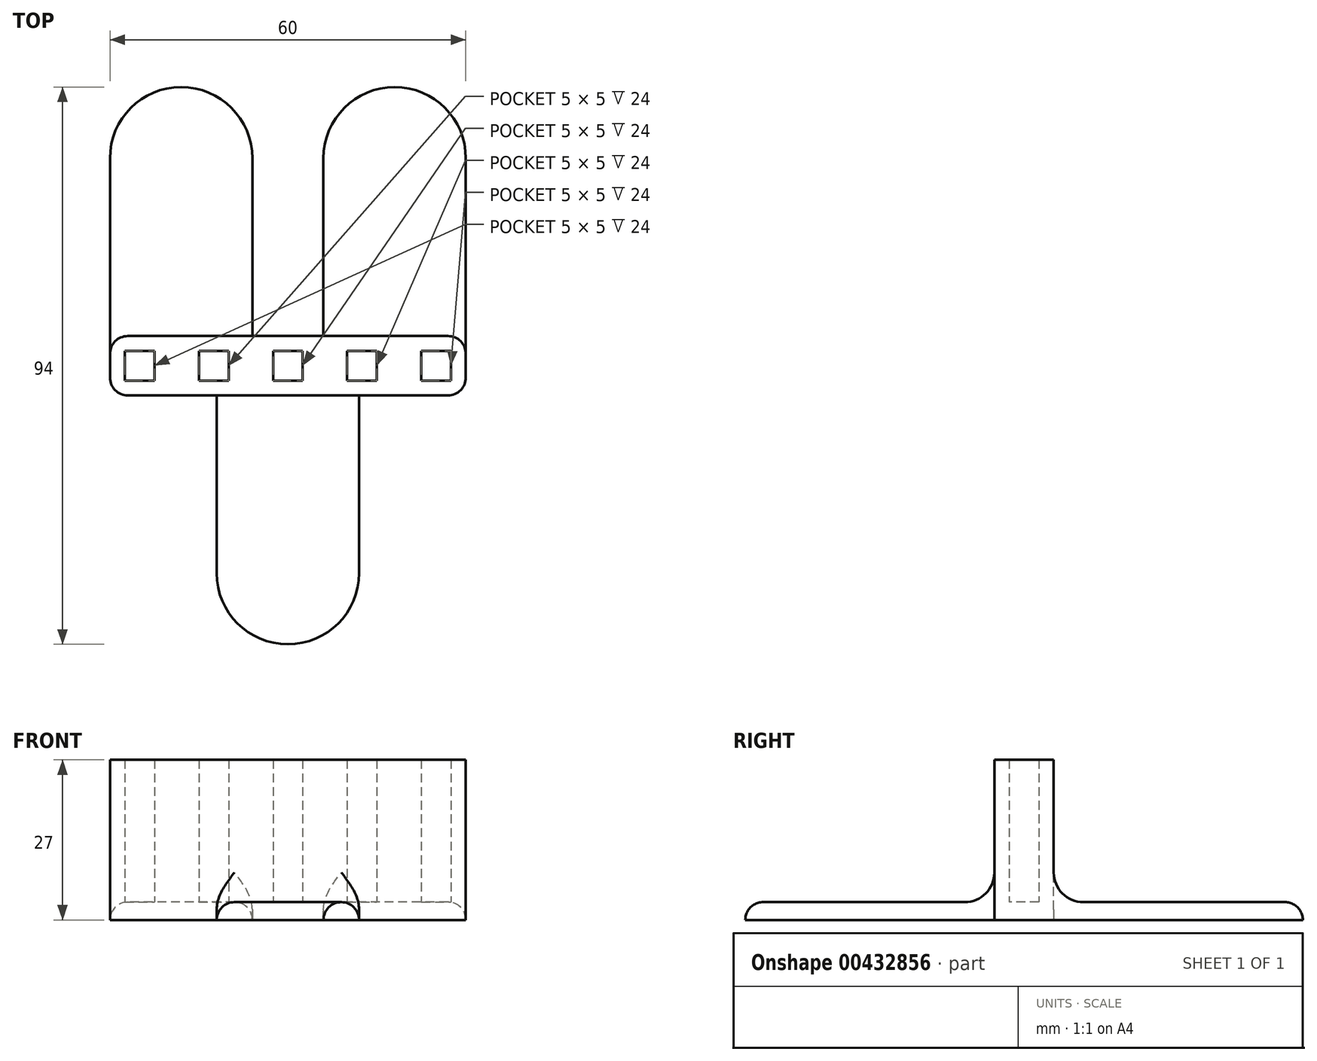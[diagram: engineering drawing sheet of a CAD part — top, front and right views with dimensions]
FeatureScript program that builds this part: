
annotation { "Feature Type Name" : "Feature", "Feature Type Description" : "" }
export const myFeature = defineFeature(function(context is Context, id is Id, definition is map)
    precondition{}
    {
        {
            var Q0;
            Q0=qCreatedBy(makeId("Top.planeOp"),FACE);
            var sketch = newSketch(context, id + "F0", { "sketchPlane" : qUnion([Q0])});
            skLineSegment(sketch, "E0.bottom", {"start": v(-12, -5) * mm, "end": v(-30, -5) * mm});
            skLineSegment(sketch, "E0.top", {"start": v(0, 5) * mm, "end": v(-6, 5) * mm});
            skLineSegment(sketch, "E0.right", {"start": v(-30, -5) * mm, "end": v(-30, 5) * mm});
            skLineSegment(sketch, "E1.left", {"start": v(-30, 5) * mm, "end": v(-30, 35) * mm});
            skLineSegment(sketch, "E1.right", {"start": v(-6, 5) * mm, "end": v(-6, 35) * mm});
            skLineSegment(sketch, "E2.right", {"start": v(-12, -5) * mm, "end": v(-12, -35) * mm});
            skArc(sketch, "E3", {"start": v(-12, -35) * mm, "mid": v(-8.49, -43.49) * mm, "end": v(0, -47) * mm});
            skArc(sketch, "E4", {"start": v(-6, 35) * mm, "mid": v(-18, 47) * mm, "end": v(-30, 35) * mm});
            skPoint(sketch, "E2.left.start.orphan", {"position": v(0, -5) * mm});
            skPoint(sketch, "E5", {"position": v(-30, 0) * mm});
            skLineSegment(sketch, "E6", {"start": v(0, -5) * mm, "end": v(0, -35) * mm, "construction": true});
            skLineSegment(sketch, "E7.MirrorCS", {"start": v(0, 5) * mm, "end": v(6, 5) * mm});
            skLineSegment(sketch, "E8.MirrorCS", {"start": v(6, 5) * mm, "end": v(6, 35) * mm});
            skArc(sketch, "E9.MirrorCS", {"start": v(6, 35) * mm, "mid": v(18, 47) * mm, "end": v(30, 35) * mm});
            skLineSegment(sketch, "E10.MirrorCS", {"start": v(30, 5) * mm, "end": v(30, 35) * mm});
            skLineSegment(sketch, "E11.MirrorCS", {"start": v(30, -5) * mm, "end": v(30, 5) * mm});
            skLineSegment(sketch, "E12.MirrorCS", {"start": v(12, -5) * mm, "end": v(30, -5) * mm});
            skLineSegment(sketch, "E13.MirrorCS", {"start": v(12, -5) * mm, "end": v(12, -35) * mm});
            skArc(sketch, "E14.MirrorCS", {"start": v(12, -35) * mm, "mid": v(8.49, -43.49) * mm, "end": v(0, -47) * mm});
            skLineSegment(sketch, "E15", {"start": v(0, 0) * mm, "end": v(-30, 0) * mm, "construction": true});
            skSolve(sketch);
        }
        {
            var Q0;
            Q0 = qSketchRegion(id + "F0", true);
            extrude(context, id + "F1", {"entities" : qUnion([Q0]), "depth" : 3 * mm});
        }
        {
            var Q0;
            Q0=makeQuery(id+"F1.opExtrude","CAP_FACE",FACE,{"disambiguationData":[OSD([sQuery(id+"F0.wireOp",EDGE,"E0.bottom"),sQuery(id+"F0.wireOp",EDGE,"E0.top"),sQuery(id+"F0.wireOp",EDGE,"E0.right"),sQuery(id+"F0.wireOp",EDGE,"E1.left"),sQuery(id+"F0.wireOp",EDGE,"E1.right"),sQuery(id+"F0.wireOp",EDGE,"E2.right"),sQuery(id+"F0.wireOp",EDGE,"E3"),sQuery(id+"F0.wireOp",EDGE,"E4"),sQuery(id+"F0.wireOp",EDGE,"E7.MirrorCS"),sQuery(id+"F0.wireOp",EDGE,"E8.MirrorCS"),sQuery(id+"F0.wireOp",EDGE,"E9.MirrorCS"),sQuery(id+"F0.wireOp",EDGE,"E10.MirrorCS"),sQuery(id+"F0.wireOp",EDGE,"E11.MirrorCS"),sQuery(id+"F0.wireOp",EDGE,"E12.MirrorCS"),sQuery(id+"F0.wireOp",EDGE,"E13.MirrorCS"),sQuery(id+"F0.wireOp",EDGE,"E14.MirrorCS")])],"isStart":false});
            var sketch = newSketch(context, id + "F2", { "sketchPlane" : qUnion([Q0])});
            skLineSegment(sketch, "E16.bottom", {"start": v(30, -5) * mm, "end": v(-30, -5) * mm});
            skLineSegment(sketch, "E16.top", {"start": v(30, 5) * mm, "end": v(-30, 5) * mm});
            skLineSegment(sketch, "E16.left", {"start": v(30, -5) * mm, "end": v(30, 5) * mm});
            skLineSegment(sketch, "E16.right", {"start": v(-30, -5) * mm, "end": v(-30, 5) * mm});
            skPoint(sketch, "E16.middle", {"position": v(0, 0) * mm});
            skLineSegment(sketch, "E17.bottom", {"start": v(-27.5, 2.5) * mm, "end": v(-22.5, 2.5) * mm});
            skLineSegment(sketch, "E17.top", {"start": v(-27.5, -2.5) * mm, "end": v(-22.5, -2.5) * mm});
            skLineSegment(sketch, "E17.left", {"start": v(-27.5, 2.5) * mm, "end": v(-27.5, -2.5) * mm});
            skLineSegment(sketch, "E17.right", {"start": v(-22.5, 2.5) * mm, "end": v(-22.5, -2.5) * mm});
            skPoint(sketch, "E17.middle", {"position": v(-25, 0) * mm});
            skLineSegment(sketch, "E18", {"start": v(0, 0) * mm, "end": v(-25, 0) * mm, "construction": true});
            skLineSegment(sketch, "E19.1.0.0", {"start": v(-10, 2.5) * mm, "end": v(-10, -2.5) * mm});
            skLineSegment(sketch, "E19.1.0.1", {"start": v(-15, -2.5) * mm, "end": v(-10, -2.5) * mm});
            skLineSegment(sketch, "E19.1.0.2", {"start": v(-15, 2.5) * mm, "end": v(-15, -2.5) * mm});
            skLineSegment(sketch, "E19.1.0.3", {"start": v(-15, 2.5) * mm, "end": v(-10, 2.5) * mm});
            skLineSegment(sketch, "E19.2.0.0", {"start": v(2.5, 2.5) * mm, "end": v(2.5, -2.5) * mm});
            skLineSegment(sketch, "E19.2.0.1", {"start": v(-2.5, -2.5) * mm, "end": v(2.5, -2.5) * mm});
            skLineSegment(sketch, "E19.2.0.2", {"start": v(-2.5, 2.5) * mm, "end": v(-2.5, -2.5) * mm});
            skLineSegment(sketch, "E19.2.0.3", {"start": v(-2.5, 2.5) * mm, "end": v(2.5, 2.5) * mm});
            skLineSegment(sketch, "E19.3.0.0", {"start": v(15, 2.5) * mm, "end": v(15, -2.5) * mm});
            skLineSegment(sketch, "E19.3.0.1", {"start": v(10, -2.5) * mm, "end": v(15, -2.5) * mm});
            skLineSegment(sketch, "E19.3.0.2", {"start": v(10, 2.5) * mm, "end": v(10, -2.5) * mm});
            skLineSegment(sketch, "E19.3.0.3", {"start": v(10, 2.5) * mm, "end": v(15, 2.5) * mm});
            skLineSegment(sketch, "E19.direction1", {"start": v(-22.5, -2.5) * mm, "end": v(-10, -2.5) * mm, "construction": true});
            skLineSegment(sketch, "E20.0.4.0", {"start": v(27.5, 2.5) * mm, "end": v(27.5, -2.5) * mm});
            skLineSegment(sketch, "E20.3.4.0", {"start": v(22.5, -2.5) * mm, "end": v(27.5, -2.5) * mm});
            skLineSegment(sketch, "E20.6.4.0", {"start": v(22.5, 2.5) * mm, "end": v(22.5, -2.5) * mm});
            skLineSegment(sketch, "E20.9.4.0", {"start": v(22.5, 2.5) * mm, "end": v(27.5, 2.5) * mm});
            skSolve(sketch);
        }
        {
            var Q0;
            Q0 = qSketchRegion(id + "F2", true);
            extrude(context, id + "F3", {"entities" : qUnion([Q0]), "operationType" : NewBodyOperationType.ADD, "depth" : 24 * mm});
        }
        {
            var Q0;
            Q0=makeQuery(id+"F3.opExtrude","CAP_EDGE",EDGE,{"disambiguationData":[OSD([sQuery(id+"F2.wireOp",EDGE,"E16.bottom")])],"isStart":true});
            var Q1;
            {var subQ2=sQuery(id+"F0.wireOp",EDGE,"E8.MirrorCS");var subQ5=sQuery(id+"F2.wireOp",EDGE,"E16.top");Q1=makeQuery(id+"F3.boolean.opBoolean","SPLIT",EDGE,{"disambiguationData":[TD([makeQuery(id+"F1.opExtrude","SWEPT_FACE",FACE,{"disambiguationData":[OSD([subQ2])]})])],"derivedFrom":makeQuery(id+"F3.opExtrude","CAP_EDGE",EDGE,{"disambiguationData":[OSD([subQ5])],"isStart":true})});}
            var Q2;
            {var subQ0=sQuery(id+"F0.wireOp",EDGE,"E1.right");var subQ3=sQuery(id+"F2.wireOp",EDGE,"E16.top");Q2=makeQuery(id+"F3.boolean.opBoolean","SPLIT",EDGE,{"disambiguationData":[TD([makeQuery(id+"F1.opExtrude","SWEPT_FACE",FACE,{"disambiguationData":[OSD([subQ0])]})])],"derivedFrom":makeQuery(id+"F3.opExtrude","CAP_EDGE",EDGE,{"disambiguationData":[OSD([subQ3])],"isStart":true})});}
            fillet(context, id + "F4", {"entities" : qUnion([Q0, Q1, Q2]), "radius" : 5 * mm, "tangentPropagation" : true, "allowEdgeOverflow" : false});
        }
        {
            var Q0;
            Q0=makeQuery(id+"F1.opExtrude","CAP_EDGE",EDGE,{"disambiguationData":[OSD([sQuery(id+"F0.wireOp",EDGE,"E13.MirrorCS")])],"isStart":false});
            var Q1;
            Q1=makeQuery(id+"F4.opFillet","BLEND_EDGE",EDGE,{"blendedFrom":[makeQuery(id+"F3.opExtrude","CAP_EDGE",EDGE,{"disambiguationData":[OSD([sQuery(id+"F2.wireOp",EDGE,"E16.bottom")])],"isStart":true}),makeQuery(id+"F1.opExtrude","SWEPT_FACE",FACE,{"disambiguationData":[OSD([sQuery(id+"F0.wireOp",EDGE,"E13.MirrorCS")])]})],"blendedInto":[makeQuery(id+"F1.opExtrude","SWEPT_FACE",FACE,{"disambiguationData":[OSD([sQuery(id+"F0.wireOp",EDGE,"E13.MirrorCS")])]})]});
            var Q2;
            Q2=makeQuery(id+"F1.opExtrude","CAP_EDGE",EDGE,{"disambiguationData":[OSD([sQuery(id+"F0.wireOp",EDGE,"E3"),sQuery(id+"F0.wireOp",EDGE,"E14.MirrorCS")])],"isStart":false});
            var Q3;
            Q3=makeQuery(id+"F1.opExtrude","CAP_EDGE",EDGE,{"disambiguationData":[OSD([sQuery(id+"F0.wireOp",EDGE,"E2.right")])],"isStart":false});
            var Q4;
            Q4=makeQuery(id+"F4.opFillet","BLEND_EDGE",EDGE,{"blendedFrom":[makeQuery(id+"F3.opExtrude","CAP_EDGE",EDGE,{"disambiguationData":[OSD([sQuery(id+"F2.wireOp",EDGE,"E16.bottom")])],"isStart":true}),makeQuery(id+"F1.opExtrude","SWEPT_FACE",FACE,{"disambiguationData":[OSD([sQuery(id+"F0.wireOp",EDGE,"E2.right")])]})],"blendedInto":[makeQuery(id+"F1.opExtrude","SWEPT_FACE",FACE,{"disambiguationData":[OSD([sQuery(id+"F0.wireOp",EDGE,"E2.right")])]})]});
            var Q5;
            Q5=makeQuery(id+"F1.opExtrude","CAP_EDGE",EDGE,{"disambiguationData":[OSD([sQuery(id+"F0.wireOp",EDGE,"E10.MirrorCS"),sQuery(id+"F0.wireOp",EDGE,"E11.MirrorCS")])],"isStart":false});
            var Q6;
            Q6=makeQuery(id+"F1.opExtrude","CAP_EDGE",EDGE,{"disambiguationData":[OSD([sQuery(id+"F0.wireOp",EDGE,"E0.right"),sQuery(id+"F0.wireOp",EDGE,"E1.left")])],"isStart":false});
            var Q7;
            Q7=makeQuery(id+"F3.boolean.opBoolean","MERGE",EDGE,{"derivedFrom":[makeQuery(id+"F1.opExtrude","SWEPT_EDGE",EDGE,{"disambiguationData":[OSD([sQuery(id+"F0.wireOp",EDGE,"E11.MirrorCS"),sQuery(id+"F0.wireOp",EDGE,"E12.MirrorCS")])]}),makeQuery(id+"F3.opExtrude","SWEPT_EDGE",EDGE,{"disambiguationData":[OSD([sQuery(id+"F2.wireOp",EDGE,"E16.bottom"),sQuery(id+"F2.wireOp",EDGE,"E16.left")])]})]});
            var Q8;
            Q8=makeQuery(id+"F3.boolean.opBoolean","MERGE",EDGE,{"derivedFrom":[makeQuery(id+"F1.opExtrude","SWEPT_EDGE",EDGE,{"disambiguationData":[OSD([sQuery(id+"F0.wireOp",EDGE,"E0.bottom"),sQuery(id+"F0.wireOp",EDGE,"E0.right")])]}),makeQuery(id+"F3.opExtrude","SWEPT_EDGE",EDGE,{"disambiguationData":[OSD([sQuery(id+"F2.wireOp",EDGE,"E16.bottom"),sQuery(id+"F2.wireOp",EDGE,"E16.right")])]})]});
            fillet(context, id + "F5", {"entities" : qUnion([Q0, Q1, Q2, Q3, Q4, Q5, Q6, Q7, Q8]), "radius" : 3 * mm, "tangentPropagation" : true, "allowEdgeOverflow" : false});
        }
    });
